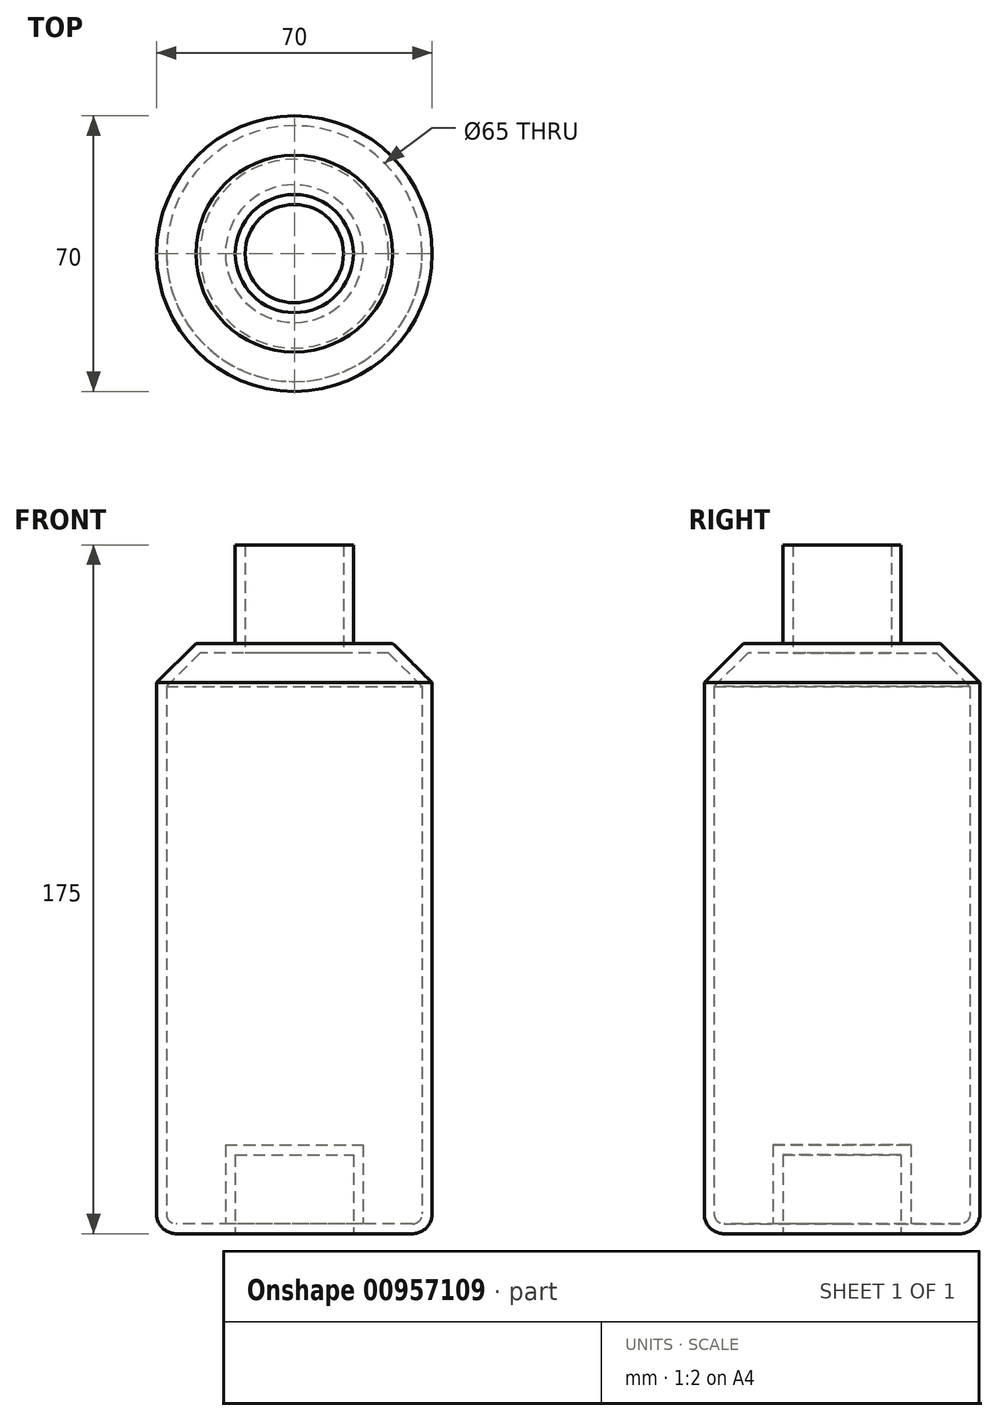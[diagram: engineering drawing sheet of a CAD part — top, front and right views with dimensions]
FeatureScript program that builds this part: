
annotation { "Feature Type Name" : "Feature", "Feature Type Description" : "" }
export const myFeature = defineFeature(function(context is Context, id is Id, definition is map)
    precondition{}
    {
        {
            var Q0;
            Q0=qCreatedBy(makeId("Top.planeOp"),FACE);
            var sketch = newSketch(context, id + "F0", { "sketchPlane" : qUnion([Q0])});
            skCircle(sketch, "E0", {"center": v(0, 0) * mm, "radius": 35 * mm});
            skSolve(sketch);
        }
        {
            var Q0;
            Q0=makeQuery(id+"F0.imprint","IMPRINT",FACE,{"disambiguationData":[TD([[makeQuery(id+"F0.imprint","IMPRINT",EDGE,{"derivedFrom":sQuery(id+"F0.wireOp",EDGE,"E0")}),1.0]])]});
            var Q1;
            Q1=sQuery(id+"F0.wireOp",EDGE,"E0");
            extrude(context, id + "F1", {"entities" : qUnion([Q0]), "surfaceEntities" : qUnion([Q1]), "depth" : 150 * mm, "offsetDistance" : 25 * mm});
        }
        {
            var Q0;
            Q0=makeQuery(id+"F1.opExtrude","CAP_FACE",FACE,{"disambiguationData":[OSD([sQuery(id+"F0.wireOp",EDGE,"E0")])],"isStart":false});
            var sketch = newSketch(context, id + "F2", { "sketchPlane" : qUnion([Q0])});
            skCircle(sketch, "E1", {"center": v(0, 0) * mm, "radius": 15 * mm});
            skSolve(sketch);
        }
        {
            var Q0;
            Q0 = qSketchRegion(id + "F2", true);
            extrude(context, id + "F3", {"entities" : qUnion([Q0]), "operationType" : NewBodyOperationType.ADD, "depth" : 25 * mm, "offsetDistance" : 25 * mm});
        }
        {
            var Q0;
            Q0=makeQuery(id+"F1.opExtrude","CAP_EDGE",EDGE,{"disambiguationData":[OSD([sQuery(id+"F0.wireOp",EDGE,"E0")])],"isStart":true});
            fillet(context, id + "F4", {"entities" : qUnion([Q0]), "radius" : 5 * mm, "tangentPropagation" : true, "allowEdgeOverflow" : false});
        }
        {
            var Q0;
            Q0=makeQuery(id+"F1.opExtrude","CAP_FACE",FACE,{"disambiguationData":[OSD([sQuery(id+"F0.wireOp",EDGE,"E0")])],"isStart":true});
            var sketch = newSketch(context, id + "F5", { "sketchPlane" : qUnion([Q0])});
            skCircle(sketch, "E2", {"center": v(0, 0) * mm, "radius": 15 * mm});
            skSolve(sketch);
        }
        {
            var Q0;
            Q0=makeQuery(id+"F5.imprint","IMPRINT",FACE,{"disambiguationData":[TD([[makeQuery(id+"F5.imprint","IMPRINT",EDGE,{"derivedFrom":sQuery(id+"F5.wireOp",EDGE,"E2")}),1.0]])]});
            var Q1;
            Q1=sQuery(id+"F5.wireOp",EDGE,"E2");
            extrude(context, id + "F6", {"entities" : qUnion([Q0]), "operationType" : NewBodyOperationType.REMOVE, "surfaceEntities" : qUnion([Q1]), "oppositeDirection" : true, "depth" : 20 * mm, "offsetDistance" : 25 * mm});
        }
        {
            var Q0;
            Q0=makeQuery(id+"F1.opExtrude","CAP_EDGE",EDGE,{"disambiguationData":[OSD([sQuery(id+"F0.wireOp",EDGE,"E0")])],"isStart":false});
            var Q1;
            Q1=makeQuery(id+"F3.opExtrude","CAP_EDGE",EDGE,{"disambiguationData":[OSD([sQuery(id+"F2.wireOp",EDGE,"E1")])],"isStart":true});
            chamfer(context, id + "F7", {"entities" : qUnion([Q0, Q1]), "width" : 10 * mm, "tangentPropagation" : true});
        }
        {
            var Q0;
            Q0=makeQuery(id+"F3.opExtrude","CAP_FACE",FACE,{"disambiguationData":[OSD([sQuery(id+"F2.wireOp",EDGE,"E1")])],"isStart":false});
            shell(context, id + "F8", {"entities" : qUnion([Q0]), "thickness" : 2.5 * mm});
        }
    });
